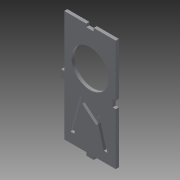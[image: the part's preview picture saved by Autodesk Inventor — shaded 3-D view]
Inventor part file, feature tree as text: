
AUTODESK INVENTOR PART (.ipt)
format: ipt  version: 2015 (Build 190159000, 159)  size: 167,424 bytes
history: native  units: in
note: dims shown in document units (in); Inventor stores cm internally (conversion verified against a paired STEP export)
features: extrude x5, sketch x5
ambient origin geometry x8: Origin, YZ Plane, XZ Plane, XY Plane, X Axis, Y Axis, Z Axis, Center Point
bodies: Solid1 (feature_tree)
feature tree (10):
  extrude  "Extrusion1"  Depth=2.084in
  sketch  "Sketch2"  dims[d2=0.125in d3=0.0in d4=0.15in]
  extrude  "Extrusion2"  Depth=0.15in
  extrude  "Extrusion3"  Depth=0.125in
  sketch  "Sketch3"  dims[d5=0.3in d6=0.125in]
  sketch  "Sketch4"  dims[d7=0.15in d8=0.3in]
  sketch  "Sketch5"  dims[d9=0.125in d13=0.3in d14=0.15in d15=0.125in d16=0.125in d17=0.0in d18=0.125in d19=0.0in d20=0.3in d21=0.15in d22=0.125in d23=1.5in d24=3.0in d25=1.041in d26=0.15in d27=0.15in d29=0.15in d31=75.0deg d32=1.5in d33=0.25in d34=75.0deg d35=0.15in d36=1.15in d38=0.4466in d39=0.2in d40=1.0in d41=0.0in d42=0.1in d43=0.0in]
  extrude  "Extrusion4"  Depth=0.3in
  extrude  "Extrusion5"  Depth=0.3in
  sketch  "Sketch1"  dims[d0=4.5in d1=2.084in]
